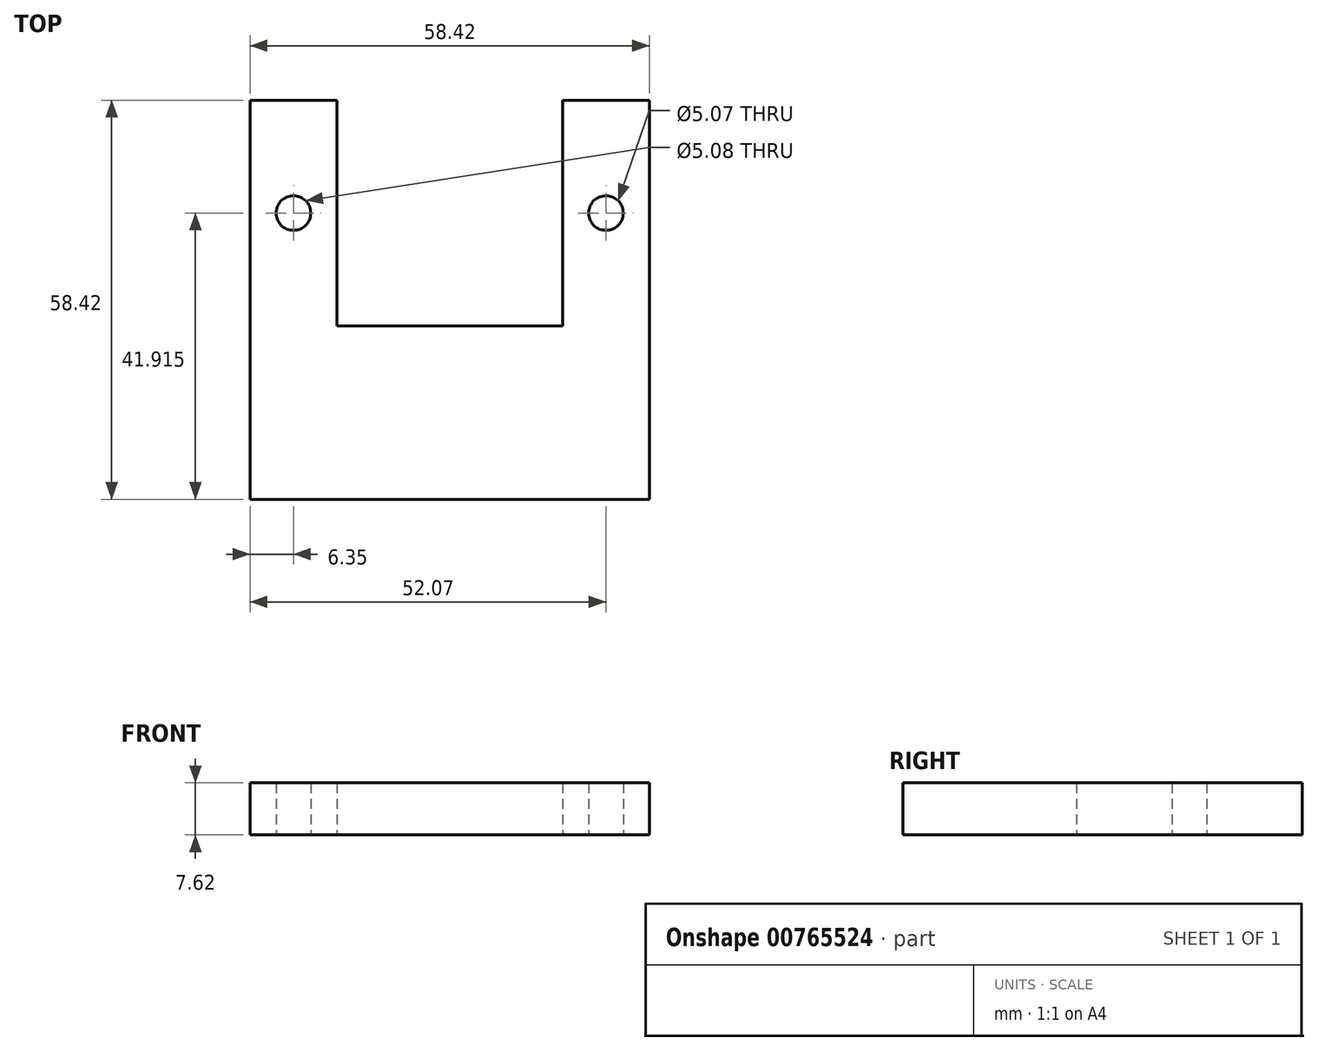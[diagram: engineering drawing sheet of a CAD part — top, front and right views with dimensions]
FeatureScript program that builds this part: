
annotation { "Feature Type Name" : "Feature", "Feature Type Description" : "" }
export const myFeature = defineFeature(function(context is Context, id is Id, definition is map)
    precondition{}
    {
        {
            var Q0;
            Q0=qCreatedBy(makeId("Top.planeOp"),FACE);
            var sketch = newSketch(context, id + "F0", { "sketchPlane" : qUnion([Q0])});
            skLineSegment(sketch, "E0.bottom", {"start": v(-29.21, 15.95) * mm, "end": v(29.2, 15.95) * mm});
            skLineSegment(sketch, "E0.top", {"start": v(-29.21, -9.45) * mm, "end": v(29.2, -9.45) * mm});
            skLineSegment(sketch, "E0.left", {"start": v(-29.21, 15.95) * mm, "end": v(-29.21, -9.45) * mm});
            skLineSegment(sketch, "E0.right", {"start": v(29.2, 15.95) * mm, "end": v(29.2, -9.45) * mm});
            skLineSegment(sketch, "E1.bottom", {"start": v(-29.21, 15.95) * mm, "end": v(-16.51, 15.95) * mm});
            skLineSegment(sketch, "E1.top", {"start": v(-29.21, 48.97) * mm, "end": v(-16.51, 48.97) * mm});
            skLineSegment(sketch, "E1.left", {"start": v(-29.21, 15.95) * mm, "end": v(-29.21, 48.97) * mm});
            skLineSegment(sketch, "E1.right", {"start": v(-16.51, 15.95) * mm, "end": v(-16.51, 48.97) * mm});
            skLineSegment(sketch, "E2.bottom", {"start": v(29.2, 15.95) * mm, "end": v(16.5, 15.95) * mm});
            skLineSegment(sketch, "E2.top", {"start": v(29.2, 48.97) * mm, "end": v(16.5, 48.97) * mm});
            skLineSegment(sketch, "E2.left", {"start": v(29.2, 15.95) * mm, "end": v(29.2, 48.97) * mm});
            skLineSegment(sketch, "E2.right", {"start": v(16.5, 15.95) * mm, "end": v(16.5, 48.97) * mm});
            skLineSegment(sketch, "E3", {"start": v(22.86, 48.97) * mm, "end": v(22.86, 15.95) * mm});
            skCircle(sketch, "E4", {"center": v(22.86, 32.46) * mm, "radius": 2.54 * mm});
            skLineSegment(sketch, "E5", {"start": v(-22.86, 48.97) * mm, "end": v(-22.86, 15.95) * mm});
            skCircle(sketch, "E6", {"center": v(-22.86, 32.46) * mm, "radius": 2.54 * mm});
            skSolve(sketch);
        }
        {
            var Q0;
            Q0 = qSketchRegion(id + "F0", true);
            extrude(context, id + "F1", {"entities" : qUnion([Q0]), "depth" : 7.62 * mm, "offsetDistance" : 25.4 * mm});
        }
    });
